FCSTD DOCUMENT  (FreeCAD 0.19R24348 (Git))
Label: SecondTry
License: All rights reserved
LicenseURL: http://en.wikipedia.org/wiki/All_rights_reserved
objects: Sketcher::SketchObject×1, Spreadsheet::Sheet×1
note: 1 computed .brp shape members not serialized (recipe doc carries the construction recipe); baked Part::Feature solids carry a one-line shape summary decoded from their .brp

FEATURE [Sketcher::SketchObject] Sketch
  FullyConstrained = false
  sketch-geometry (8):
    g0: LineSegment StartX=0 StartY=105.561 StartZ=0 EndX=0 EndY=9.98967 EndZ=0
    g1: LineSegment StartX=9.98967 StartY=0 StartZ=0 EndX=115.489 EndY=0 EndZ=0
    g2: LineSegment StartX=0 StartY=9.98967 StartZ=0 EndX=9.98967 EndY=0 EndZ=0
    g3: LineSegment StartX=0 StartY=0 StartZ=0 EndX=0 EndY=9.98967 EndZ=0
    g4: LineSegment StartX=0 StartY=0 StartZ=0 EndX=9.98967 EndY=0 EndZ=0
    g5: Circle CenterX=-11.8936 CenterY=143.393 CenterZ=0 NormalX=0 NormalY=0 NormalZ=1 AngleXU=0 Radius=21.9002
    g6: Circle CenterX=-15.9455 CenterY=112.257 CenterZ=0 NormalX=0 NormalY=0 NormalZ=1 AngleXU=0 Radius=12.3413
    g7: Circle CenterX=15.4033 CenterY=161.306 CenterZ=0 NormalX=0 NormalY=0 NormalZ=1 AngleXU=0 Radius=10.5729
  constraints (11):
    c: Vertical(g0)
    c: Horizontal(g1)
    c: Coincident(g1,g2)
    c: Coincident(g0,g2)
    c: Angle(g-2,g2) = 0.785398
    c: Coincident(g3,g-1)
    c: Coincident(g3,g0)
    c: Vertical(g3)
    c: Coincident(g4,g-1)
    c: Coincident(g4,g1)
    c: Horizontal(g4)
FEATURE [Spreadsheet::Sheet] Spreadsheet  label="Parameters"
  cells = A1=D_1; B1(D_1)=27; A2=KAT; B2(KAT)=14; A3=KAT_2; B3=28; A4=KPX; B4=69; A5=KPY; B5=45; A6=D_2; B6=39; A7=RKK_1; B7=6; A8=KOX; B8=53; A9=KOY; B9=53; A10=WX_1; B10(WX_1)=106; A11=WX_2; B11(WX_2)=136; A12=WY_1; B12(WY_1)=106; A13=RW_1; B13(RW_1)=6; A14=RW_2; B14(RW_2)=14; A15=RW_3; B15(RW_3)=27; A16=RW_4; B16(RW_4)=6; A17=RW_5; B17=6; A18=RW_6; B18=13; A19=FW_1; B19=6; A20=FW_2; B20=5.5; A21=KX_1; B21=12; A22=KX_2; B22=17; A23=KX_3; B23=68; A24=KX_4; B24=139; A25=KX_5; B25=168; A26=KX_6; B26=180; A27=KY_1; B27=12; A28=KY_2; B28=38; A29=KY_3; B29=109; A30=KY_4; B30=146; A31=KY_5; B31=154; A32=KY_6; B32=166; A33=FK_1; B33=2; A34=RK_1; B34=2; A35=H_1; B35=12; A36=H_2; B36=18; A37=KH_1; B37=10; A38=KH_2; B38=6; A39=OTWX_1; B39=9; A40=OTWY_1; B40=7; A41=OTWY_2; B41=14; A42=GOTW_1; B42=14; A43=GOTW_2; B43=10; A44=WY_1_1; B44(WY_1_1)=19.0787840283389
